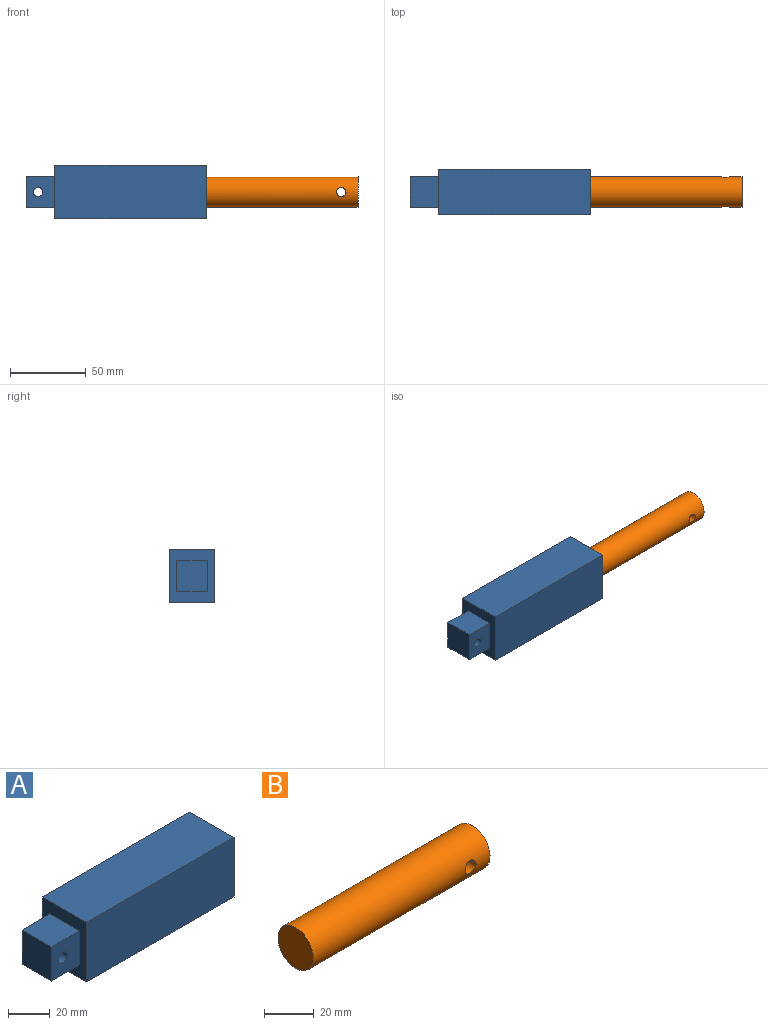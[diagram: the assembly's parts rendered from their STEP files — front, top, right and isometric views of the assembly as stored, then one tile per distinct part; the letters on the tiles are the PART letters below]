
ASSEMBLY  parts=2 mates=1
PART A: 12 faces, bbox 119x30x35 mm
  f0: plane 20x19mm, normal (0,0,1), area 380mm2, adj f1,f4,f5,f6
  f1: plane 20x20mm, normal (-1,0,0), area 400mm2, adj f0,f2,f4,f5
  f2: plane 20x19mm, normal (0,0,-1), area 380mm2, adj f1,f4,f5,f6
  f3: cylinder r=3.1mm len=20mm, axis (0,1,0), area 389.6mm2, adj f4,f5
  f4: plane 20x19mm, normal (0,-1,0), area 349.8mm2, adj f0,f1,f2,f3,f6
  f5: plane 20x19mm, normal (0,1,0), area 349.8mm2, adj f0,f1,f2,f3,f6
  f6: plane 35x30mm, normal (-1,0,0), area 650mm2, adj f0,f2,f4,f5,f7,f9,f10,f11
  f7: plane 100x30mm, normal (0,0,-1), area 3000mm2, adj f6,f8,f10,f11
  f8: plane 35x30mm, normal (1,0,0), area 1050mm2, adj f7,f9,f10,f11
  f9: plane 100x30mm, normal (0,0,1), area 3000mm2, adj f6,f8,f10,f11
  f10: plane 100x35mm, normal (0,-1,0), area 3500mm2, adj f6,f7,f8,f9
  f11: plane 100x35mm, normal (0,1,0), area 3500mm2, adj f6,f7,f8,f9
PART B: 4 faces, bbox 100x20x20 mm
  f0: cylinder r=10mm len=100mm, axis (-1,0,0), area 6221.9mm2, adj f1,f2,f3
  f1: plane 20x20mm, normal (1,0,0), area 314.2mm2, adj f0
  f2: plane 20x20mm, normal (-1,0,0), area 314.2mm2, adj f0
  f3: cylinder r=3.1mm len=20mm, axis (0,1,0), area 380mm2, adj f0
PLACE A t=(-54.3,-8.42,46.09)mm fixed
PLACE B t=(-54.3,-8.42,46.09)mm
MATE slider A.f8 <-> B.f0  axis (1,0,0) through (-3.3,-8.42,46.09)mm
